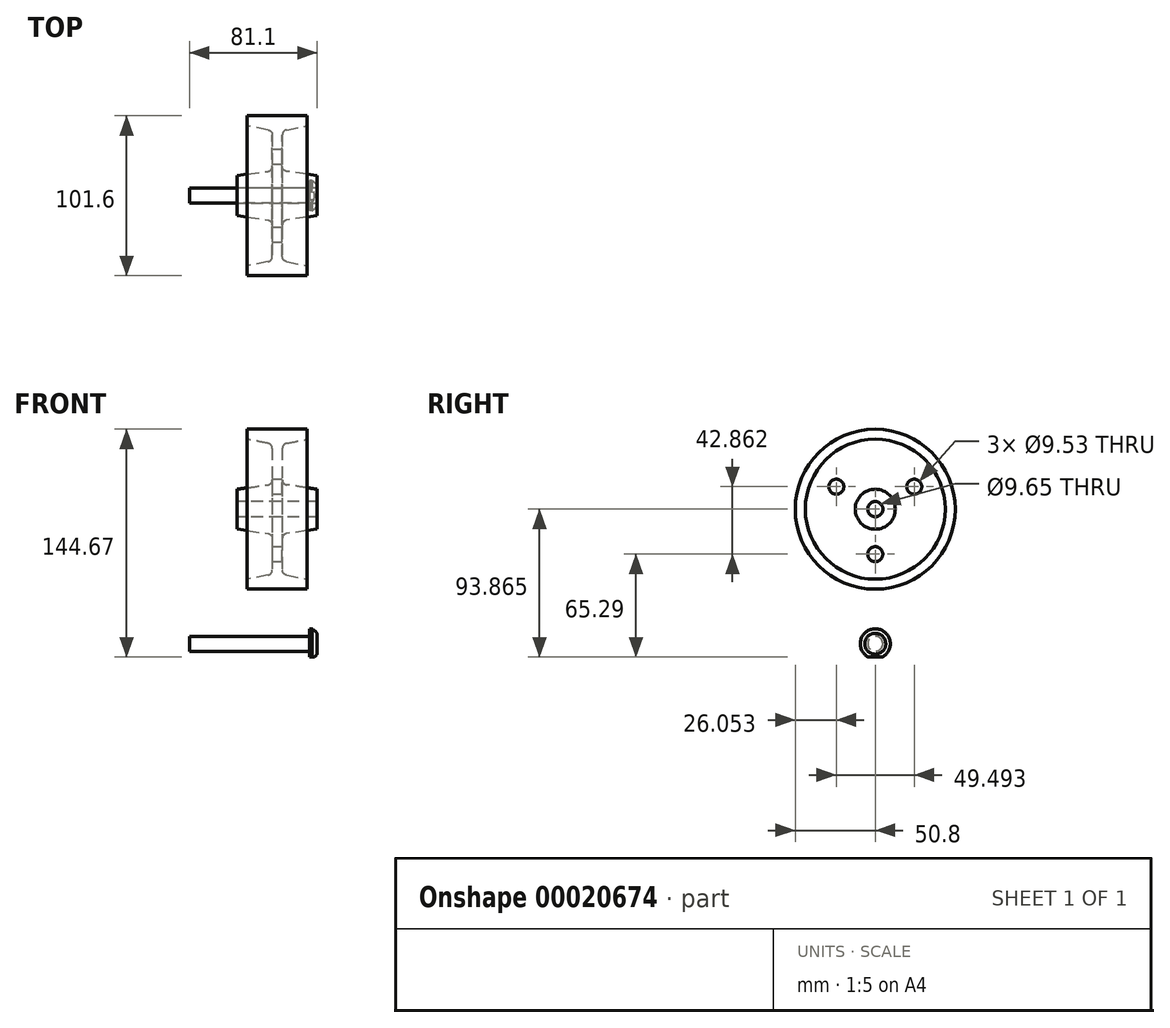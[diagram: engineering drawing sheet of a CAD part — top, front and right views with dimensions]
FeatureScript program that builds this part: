
annotation { "Feature Type Name" : "Feature", "Feature Type Description" : "" }
export const myFeature = defineFeature(function(context is Context, id is Id, definition is map)
    precondition{}
    {
        {
            var Q0;
            Q0=qCreatedBy(makeId("Front.planeOp"),FACE);
            var sketch = newSketch(context, id + "F0", { "sketchPlane" : qUnion([Q0])});
            skLineSegment(sketch, "E0", {"start": v(-25.4, 37.47) * mm, "end": v(25.4, 37.47) * mm});
            skLineSegment(sketch, "E1", {"start": v(-19.05, -8.5) * mm, "end": v(19.05, -8.5) * mm});
            skLineSegment(sketch, "E2", {"start": v(-30.22, 42.3) * mm, "end": v(30.22, 42.3) * mm, "construction": true});
            skLineSegment(sketch, "E3", {"start": v(0, 42.3) * mm, "end": v(0, 37.47) * mm, "construction": true});
            skLineSegment(sketch, "E4", {"start": v(0, 42.3) * mm, "end": v(0, 1.02) * mm, "construction": true});
            skLineSegment(sketch, "E5", {"start": v(-3.17, 37.47) * mm, "end": v(3.18, 37.47) * mm, "construction": true});
            skLineSegment(sketch, "E6", {"start": v(-3.17, 23.67) * mm, "end": v(-3.17, 3.62) * mm});
            skLineSegment(sketch, "E7", {"start": v(3.18, 23.67) * mm, "end": v(3.18, 3.62) * mm});
            skLineSegment(sketch, "E8", {"start": v(-19.05, -8.5) * mm, "end": v(-19.05, -2.15) * mm});
            skLineSegment(sketch, "E9", {"start": v(19.05, -8.5) * mm, "end": v(19.05, -2.15) * mm});
            skLineSegment(sketch, "E10", {"start": v(-25.4, 37.47) * mm, "end": v(-25.4, 29.6) * mm});
            skLineSegment(sketch, "E11", {"start": v(25.4, 37.47) * mm, "end": v(25.4, 29.6) * mm});
            skLineSegment(sketch, "E12", {"start": v(-25.4, 29.6) * mm, "end": v(25.4, 29.6) * mm, "construction": true});
            skPoint(sketch, "E13.newPointA", {"position": v(0, -2.15) * mm});
            skPoint(sketch, "E13.newPointB", {"position": v(0, -8.5) * mm});
            skLineSegment(sketch, "E14", {"start": v(-19.05, -2.15) * mm, "end": v(19.05, -2.15) * mm, "construction": true});
            skLineSegment(sketch, "E15", {"start": v(-19.05, -2.15) * mm, "end": v(-5.73, 0.5) * mm});
            skLineSegment(sketch, "E16", {"start": v(5.73, 0.5) * mm, "end": v(19.05, -2.15) * mm});
            skArc(sketch, "E17.filletArc", {"start": v(-5.73, 0.5) * mm, "mid": v(-3.9, 1.61) * mm, "end": v(-3.17, 3.62) * mm});
            skArc(sketch, "E18.filletArc", {"start": v(3.18, 3.62) * mm, "mid": v(3.9, 1.61) * mm, "end": v(5.73, 0.5) * mm});
            skLineSegment(sketch, "E19", {"start": v(-25.4, 37.47) * mm, "end": v(-25.4, 26.42) * mm, "construction": true});
            skLineSegment(sketch, "E20", {"start": v(-25.4, 29.6) * mm, "end": v(-5.9, 26.8) * mm});
            skLineSegment(sketch, "E21", {"start": v(25.4, 29.6) * mm, "end": v(5.9, 26.8) * mm});
            skArc(sketch, "E22.filletArc", {"start": v(-3.17, 23.67) * mm, "mid": v(-3.95, 25.75) * mm, "end": v(-5.9, 26.8) * mm});
            skArc(sketch, "E23.filletArc", {"start": v(5.9, 26.8) * mm, "mid": v(3.95, 25.75) * mm, "end": v(3.18, 23.67) * mm});
            skSolve(sketch);
        }
        {
            var Q0;
            Q0=makeQuery(id+"F0.imprint","IMPRINT",FACE,{"disambiguationData":[TD([[makeQuery(id+"F0.imprint","IMPRINT",EDGE,{"derivedFrom":sQuery(id+"F0.wireOp",EDGE,"E0")}),-1.0]])]});
            var Q1;
            Q1=sQuery(id+"F0.wireOp",EDGE,"E2");
            revolve(context, id + "F1", {"entities" : qUnion([Q0]), "axis" : qUnion([Q1]), "revolveType" : RevolveType.FULL});
        }
        {
            var Q0;
            Q0=qCreatedBy(makeId("Right.planeOp"),FACE);
            var sketch = newSketch(context, id + "F2", { "sketchPlane" : qUnion([Q0])});
            skCircle(sketch, "E24", {"center": v(0, 42.3) * mm, "radius": 28.58 * mm, "construction": true});
            skCircle(sketch, "E25", {"center": v(-24.75, 56.58) * mm, "radius": 4.76 * mm});
            skCircle(sketch, "E26", {"center": v(24.75, 56.58) * mm, "radius": 4.76 * mm});
            skCircle(sketch, "E27", {"center": v(0, 13.72) * mm, "radius": 4.76 * mm});
            skSolve(sketch);
        }
        {
            var Q0;
            Q0=makeQuery(id+"F1.opRevolve","SWEPT_FACE",FACE,{"disambiguationData":[OSD([sQuery(id+"F0.wireOp",EDGE,"E7")])]});
            var sketch = newSketch(context, id + "F3", { "sketchPlane" : qUnion([Q0])});
            skCircle(sketch, "E28.0", {"center": v(-24.75, 56.58) * mm, "radius": 4.76 * mm});
            skCircle(sketch, "E29.0", {"center": v(24.75, 56.58) * mm, "radius": 4.76 * mm});
            skCircle(sketch, "E30.0", {"center": v(0, 13.72) * mm, "radius": 4.76 * mm});
            skSolve(sketch);
        }
        {
            var Q0;
            Q0=makeQuery(id+"F3.imprint","IMPRINT",FACE,{"disambiguationData":[TD([[makeQuery(id+"F3.imprint","IMPRINT",EDGE,{"derivedFrom":sQuery(id+"F3.wireOp",EDGE,"E28.0")}),1.0]])]});
            var Q1;
            Q1=makeQuery(id+"F3.imprint","IMPRINT",FACE,{"disambiguationData":[TD([[makeQuery(id+"F3.imprint","IMPRINT",EDGE,{"derivedFrom":sQuery(id+"F3.wireOp",EDGE,"E29.0")}),1.0]])]});
            var Q2;
            Q2=makeQuery(id+"F3.imprint","IMPRINT",FACE,{"disambiguationData":[TD([[makeQuery(id+"F3.imprint","IMPRINT",EDGE,{"derivedFrom":sQuery(id+"F3.wireOp",EDGE,"E30.0")}),1.0]])]});
            extrude(context, id + "F4", {"entities" : qUnion([Q0, Q1, Q2]), "operationType" : NewBodyOperationType.REMOVE, "oppositeDirection" : true, "depth" : 25.4 * mm});
        }
        {
            var Q0;
            Q0=qCreatedBy(makeId("Front.planeOp"),FACE);
            var sketch = newSketch(context, id + "F5", { "sketchPlane" : qUnion([Q0])});
            skArc(sketch, "E31", {"start": v(22.08, -52.72) * mm, "mid": v(23.81, -51.44) * mm, "end": v(25.26, -49.85) * mm});
            skLineSegment(sketch, "E32", {"start": v(9.53, -52.72) * mm, "end": v(9.53, -52.72) * mm});
            skLineSegment(sketch, "E33", {"start": v(20.2, -38.43) * mm, "end": v(20.5, -38.43) * mm});
            skLineSegment(sketch, "E34", {"start": v(9.53, -47.95) * mm, "end": v(-55.7, -47.95) * mm});
            skLineSegment(sketch, "E35", {"start": v(-55.7, -43.2) * mm, "end": v(-55.7, -47.95) * mm});
            skLineSegment(sketch, "E36", {"start": v(25.26, -43.2) * mm, "end": v(-55.7, -43.2) * mm});
            skLineSegment(sketch, "E37", {"start": v(9.53, -47.95) * mm, "end": v(9.53, -43.2) * mm});
            skLineSegment(sketch, "E38.4", {"start": v(-55.7, -43.2) * mm, "end": v(20.5, -43.2) * mm});
            skLineSegment(sketch, "E38.8", {"start": v(20.5, -43.2) * mm, "end": v(25.26, -43.2) * mm});
            skLineSegment(sketch, "E38.9", {"start": v(20.5, -43.2) * mm, "end": v(22.08, -43.2) * mm});
            skLineSegment(sketch, "E38.11", {"start": v(22.08, -43.2) * mm, "end": v(22.08, -52.72) * mm});
            skLineSegment(sketch, "E38.14", {"start": v(25.26, -43.2) * mm, "end": v(25.26, -49.85) * mm});
            skPoint(sketch, "E38.10.end.orphan", {"position": v(22.08, -33.67) * mm});
            skPoint(sketch, "E38.10.start.orphan", {"position": v(22.08, -43.2) * mm});
            skPoint(sketch, "E38.15.end.orphan", {"position": v(22.08, -33.67) * mm});
            skPoint(sketch, "E38.15.start.orphan", {"position": v(25.26, -36.54) * mm});
            skPoint(sketch, "E38.13.end.orphan", {"position": v(25.26, -36.54) * mm});
            skPoint(sketch, "E38.13.start.orphan", {"position": v(25.26, -43.2) * mm});
            skPoint(sketch, "E38.6.end.orphan", {"position": v(20.5, -43.2) * mm});
            skPoint(sketch, "E38.7.start.orphan", {"position": v(20.5, -38.43) * mm});
            skPoint(sketch, "E38.2.end.orphan", {"position": v(20.5, -38.43) * mm});
            skPoint(sketch, "E38.2.start.orphan", {"position": v(20.5, -40.81) * mm});
            skPoint(sketch, "E38.3.start.orphan", {"position": v(-55.7, -38.43) * mm});
            skPoint(sketch, "E39.orphan", {"position": v(-55.7, -38.43) * mm});
            skPoint(sketch, "E38.5.end.orphan", {"position": v(-55.7, -43.2) * mm});
            skPoint(sketch, "E38.5.start.orphan", {"position": v(-55.7, -38.43) * mm});
            skPoint(sketch, "E38.1.end.orphan", {"position": v(-55.7, -38.43) * mm});
            skPoint(sketch, "E38.1.start.orphan", {"position": v(-55.7, -43.2) * mm});
            skLineSegment(sketch, "E40", {"start": v(20.5, -43.2) * mm, "end": v(20.5, -52.72) * mm});
            skLineSegment(sketch, "E41", {"start": v(22.08, -52.72) * mm, "end": v(20.5, -52.72) * mm});
            skLineSegment(sketch, "E42", {"start": v(9.53, -47.95) * mm, "end": v(20.5, -47.95) * mm});
            skPoint(sketch, "E43", {"position": v(23.66, -51.57) * mm});
            skPoint(sketch, "E44", {"position": v(20.5, -51.57) * mm});
            skSolve(sketch);
        }
        {
            var Q0;
            Q0 = qSketchRegion(id + "F5", true);
            var Q1;
            Q1=sQuery(id+"F5.wireOp",EDGE,"E38.4");
            revolve(context, id + "F6", {"entities" : qUnion([Q0]), "axis" : qUnion([Q1]), "revolveType" : RevolveType.FULL});
        }
        {
            var Q0;
            Q0=makeQuery(id+"F6.opRevolve","SWEPT_FACE",FACE,{"disambiguationData":[OSD([sQuery(id+"F5.wireOp",EDGE,"E38.14")])]});
            cPlane(context, id + "F7", {"entities" : qUnion([Q0]), "cplaneType" : CPlaneType.OFFSET, "offset" : 0 * mm, "width" : 152.4 * mm, "height" : 152.4 * mm});
        }
        {
            var Q0;
            Q0=qCreatedBy(id+"F7.planeOp",FACE);
            var sketch = newSketch(context, id + "F8", { "sketchPlane" : qUnion([Q0])});
            skCircle(sketch, "E45", {"center": v(0, -43.2) * mm, "radius": 3.55 * mm});
            skLineSegment(sketch, "E46", {"start": v(0, -43.2) * mm, "end": v(0, -51.57) * mm});
            skLineSegment(sketch, "E47", {"start": v(6.72, -51.57) * mm, "end": v(-7.17, -51.57) * mm});
            skSolve(sketch);
        }
        {
            var Q0;
            Q0=makeQuery(id+"F6.opRevolve","SWEPT_FACE",FACE,{"disambiguationData":[OSD([sQuery(id+"F5.wireOp",EDGE,"E40")])]});
            cPlane(context, id + "F9", {"entities" : qUnion([Q0]), "cplaneType" : CPlaneType.OFFSET, "offset" : 0 * mm, "width" : 152.4 * mm, "height" : 152.4 * mm});
        }
        {
            var Q0;
            Q0=qCreatedBy(id+"F9.planeOp",FACE);
            var sketch = newSketch(context, id + "F10", { "sketchPlane" : qUnion([Q0])});
            skLineSegment(sketch, "E48.0", {"start": v(-6.72, -51.57) * mm, "end": v(7.17, -51.57) * mm});
            skLineSegment(sketch, "E49.bottom", {"start": v(-6.72, -51.57) * mm, "end": v(7.2, -51.57) * mm});
            skLineSegment(sketch, "E49.top", {"start": v(-6.72, -55.14) * mm, "end": v(7.2, -55.14) * mm});
            skLineSegment(sketch, "E49.left", {"start": v(-6.72, -51.57) * mm, "end": v(-6.72, -55.14) * mm});
            skLineSegment(sketch, "E49.right", {"start": v(7.2, -51.57) * mm, "end": v(7.2, -55.14) * mm});
            skSolve(sketch);
        }
        {
            var Q0;
            Q0=makeQuery(id+"F10.imprint","IMPRINT",FACE,{"disambiguationData":[TD([[makeQuery(id+"F10.imprint","IMPRINT",EDGE,{"derivedFrom":sQuery(id+"F10.wireOp",EDGE,"E49.top")}),1.0]])]});
            extrude(context, id + "F11", {"entities" : qUnion([Q0]), "operationType" : NewBodyOperationType.REMOVE, "oppositeDirection" : true, "depth" : 25.4 * mm});
        }
    });
